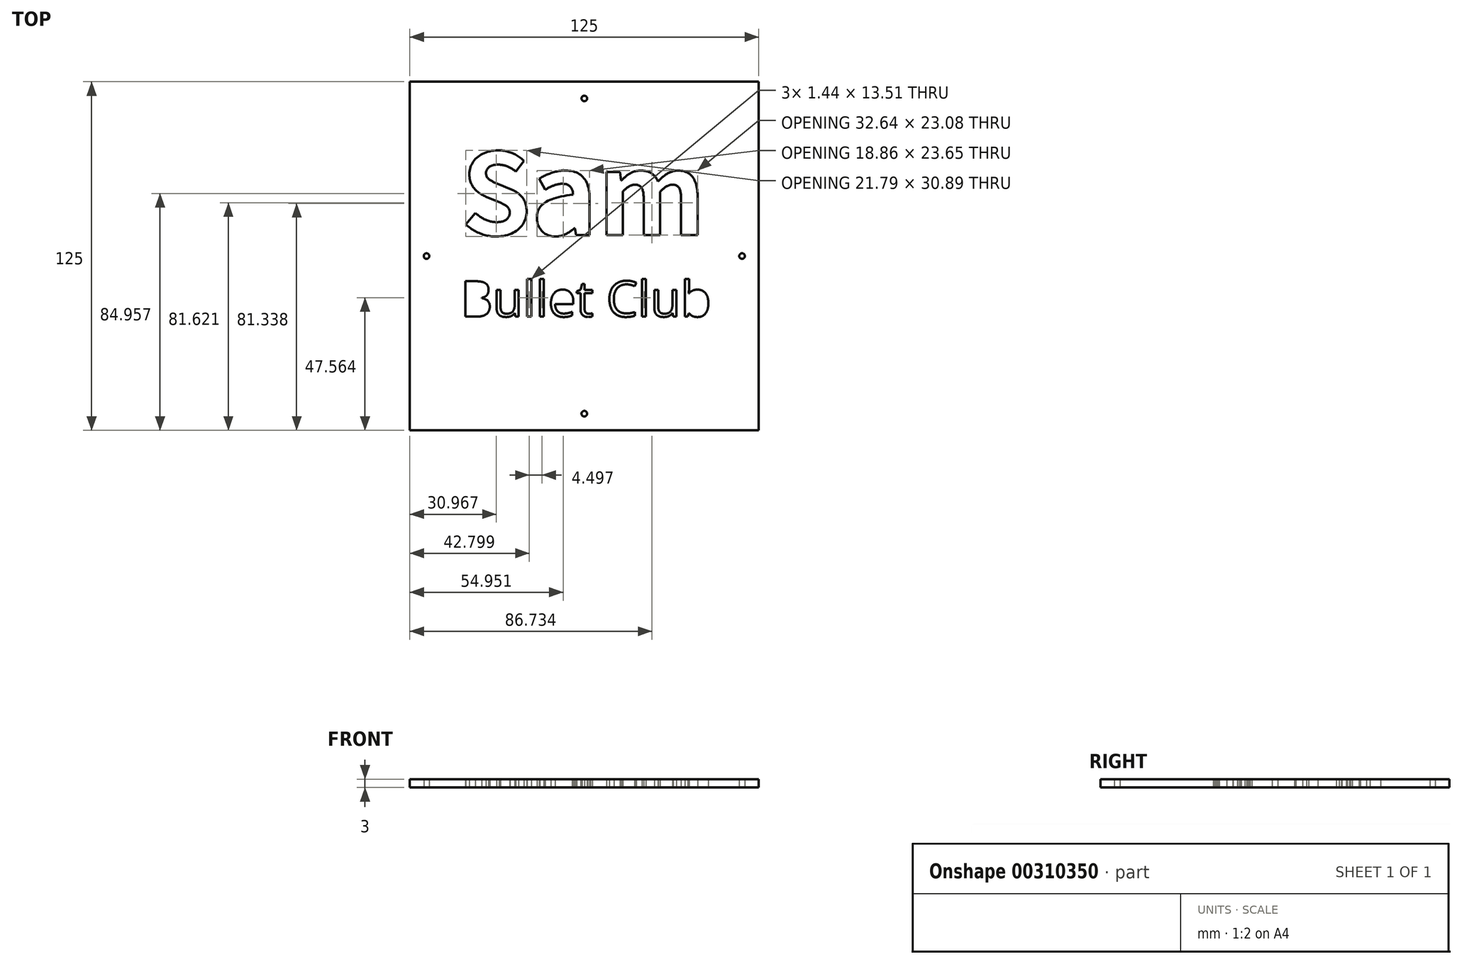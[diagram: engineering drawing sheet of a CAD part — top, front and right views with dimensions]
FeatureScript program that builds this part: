
annotation { "Feature Type Name" : "Feature", "Feature Type Description" : "" }
export const myFeature = defineFeature(function(context is Context, id is Id, definition is map)
    precondition{}
    {
        {
            var Q0;
            Q0=qCreatedBy(makeId("Top.planeOp"),FACE);
            var sketch = newSketch(context, id + "F0", { "sketchPlane" : qUnion([Q0])});
            skLineSegment(sketch, "E0.bottom", {"start": v(-45.43, 59.27) * mm, "end": v(79.57, 59.27) * mm});
            skLineSegment(sketch, "E0.top", {"start": v(-45.43, -65.73) * mm, "end": v(79.57, -65.73) * mm});
            skLineSegment(sketch, "E0.left", {"start": v(-45.43, 59.27) * mm, "end": v(-45.43, -65.73) * mm});
            skLineSegment(sketch, "E0.right", {"start": v(79.57, 59.27) * mm, "end": v(79.57, -65.73) * mm});
            skCircle(sketch, "E1", {"center": v(17.07, 53.27) * mm, "radius": 1 * mm});
            skCircle(sketch, "E2", {"center": v(-39.43, -3.23) * mm, "radius": 1 * mm});
            skCircle(sketch, "E3", {"center": v(17.07, -59.73) * mm, "radius": 1 * mm});
            skCircle(sketch, "E4", {"center": v(73.57, -3.23) * mm, "radius": 1 * mm});
            skText(sketch, "E5", { "text": "Sam", "fontName": "NotoSansCJKkr-Bold.otf"});
            skText(sketch, "E6", { "text": "Bullet Club", "fontName": "OpenSans-Regular.ttf"});
            const initialGuessF0  = {"E5": [-0.02705, 0.00435, 1, 0, 0.02895], "E6": [-0.02731, -0.02492, 1, 0, 0.0128]};
            skSetInitialGuess(sketch, initialGuessF0);
            skSolve(sketch);
        }
        {
            var Q0;
            Q0 = qSketchRegion(id + "F0", true);
            var Q1;
            Q1=makeQuery(id+"F0.imprint","IMPRINT",FACE,{"disambiguationData":[TD([[makeQuery(id+"F0.imprint","IMPRINT",EDGE,{"derivedFrom":sQuery(id+"F0.wireOp",EDGE,"E0.bottom")}),-1.0]])]});
            extrude(context, id + "F1", {"entities" : qUnion([Q0, Q1]), "depth" : 3 * mm});
        }
    });
